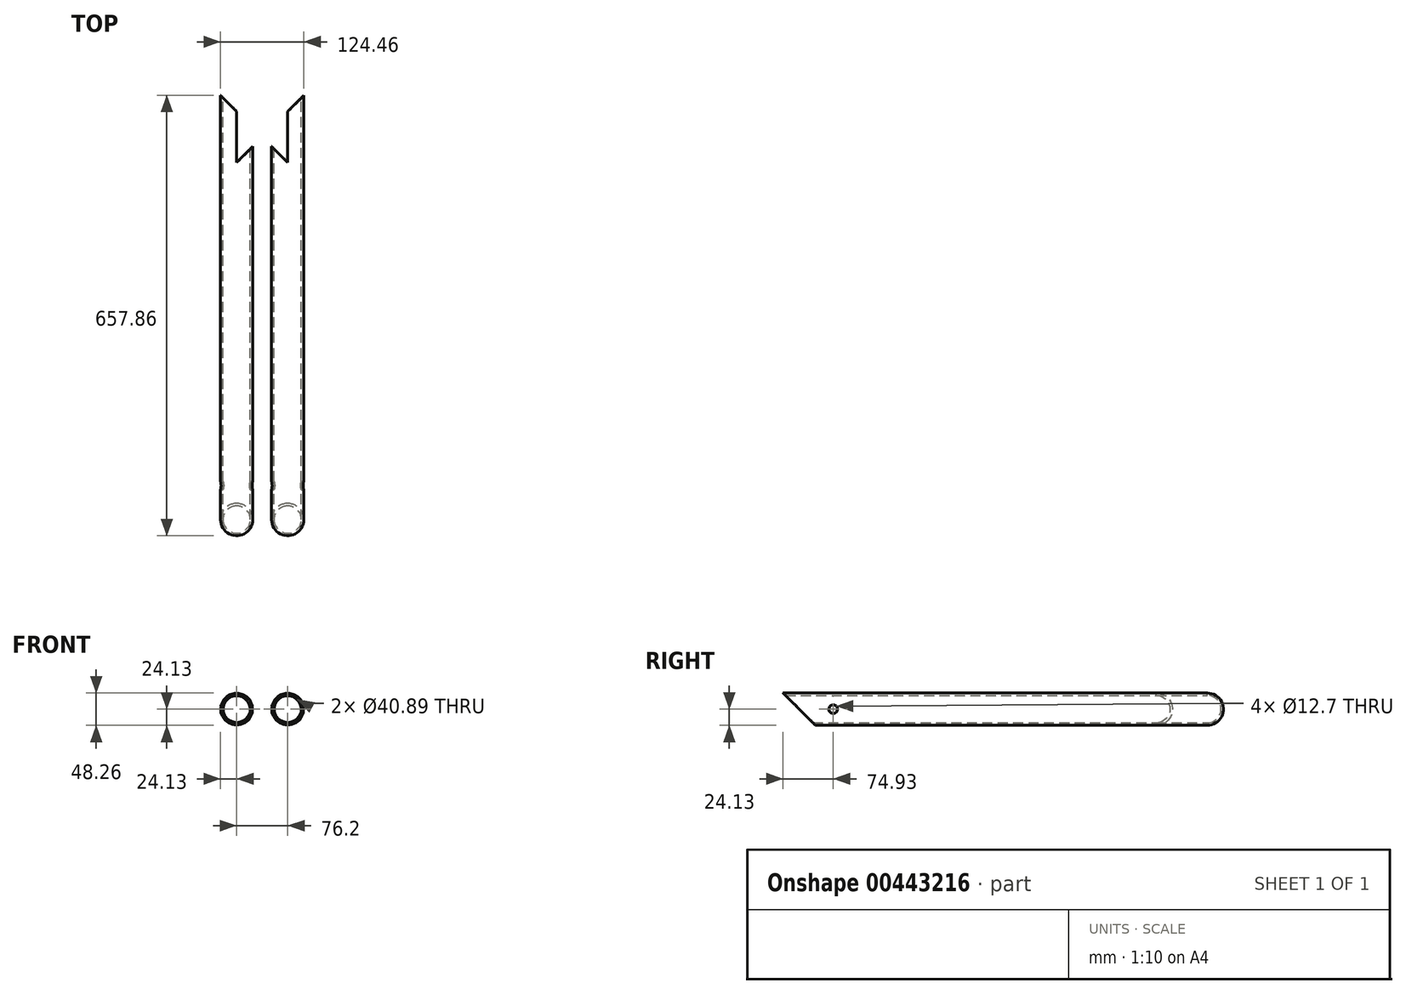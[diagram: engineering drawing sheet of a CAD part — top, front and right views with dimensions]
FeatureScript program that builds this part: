
annotation { "Feature Type Name" : "Feature", "Feature Type Description" : "" }
export const myFeature = defineFeature(function(context is Context, id is Id, definition is map)
    precondition{}
    {
        {
            var Q0;
            Q0=qCreatedBy(makeId("Front.planeOp"),FACE);
            var sketch = newSketch(context, id + "F0", { "sketchPlane" : qUnion([Q0])});
            skCircle(sketch, "E0", {"center": v(0, 0) * mm, "radius": 24.13 * mm});
            skCircle(sketch, "E1", {"center": v(0, 0) * mm, "radius": 20.45 * mm});
            skSolve(sketch);
        }
        {
            var Q0;
            Q0=makeQuery(id+"F0.imprint","IMPRINT",FACE,{"disambiguationData":[TD([[makeQuery(id+"F0.imprint","IMPRINT",EDGE,{"derivedFrom":sQuery(id+"F0.wireOp",EDGE,"E0")}),1.0]])]});
            extrude(context, id + "F1", {"entities" : qUnion([Q0]), "endBound" : BoundingType.SYMMETRIC, "depth" : 711.2 * mm});
        }
        {
            var Q0;
            Q0=qCreatedBy(makeId("Front.planeOp"),FACE);
            var sketch = newSketch(context, id + "F2", { "sketchPlane" : qUnion([Q0])});
            skCircle(sketch, "E2", {"center": v(-76.2, 0) * mm, "radius": 24.13 * mm});
            skCircle(sketch, "E3", {"center": v(-76.2, 0) * mm, "radius": 20.45 * mm});
            skSolve(sketch);
        }
        {
            var Q0;
            Q0=makeQuery(id+"F2.imprint","IMPRINT",FACE,{"disambiguationData":[TD([[makeQuery(id+"F2.imprint","IMPRINT",EDGE,{"derivedFrom":sQuery(id+"F2.wireOp",EDGE,"E2")}),1.0]])]});
            extrude(context, id + "F3", {"entities" : qUnion([Q0]), "endBound" : BoundingType.SYMMETRIC, "depth" : 711.2 * mm});
        }
        {
            var Q0;
            Q0=qCreatedBy(makeId("Right.planeOp"),FACE);
            var sketch = newSketch(context, id + "F4", { "sketchPlane" : qUnion([Q0])});
            skLineSegment(sketch, "E4", {"start": v(-304.8, 0) * mm, "end": v(-400.48, 95.68) * mm});
            skLineSegment(sketch, "E5", {"start": v(-400.48, 95.68) * mm, "end": v(-522.8, 95.68) * mm});
            skLineSegment(sketch, "E6", {"start": v(-522.8, 95.68) * mm, "end": v(-522.8, -148.2) * mm});
            skLineSegment(sketch, "E7", {"start": v(-522.8, -148.2) * mm, "end": v(-156.6, -148.2) * mm});
            skLineSegment(sketch, "E8", {"start": v(-156.6, -148.2) * mm, "end": v(-304.8, 0) * mm});
            skSolve(sketch);
        }
        {
            var Q0;
            Q0 = qSketchRegion(id + "F4", true);
            extrude(context, id + "F5", {"entities" : qUnion([Q0]), "operationType" : NewBodyOperationType.REMOVE, "endBound" : BoundingType.SYMMETRIC, "oppositeDirection" : true, "depth" : 304.8 * mm});
        }
        {
            var Q0;
            Q0=qCreatedBy(makeId("Top.planeOp"),FACE);
            var sketch = newSketch(context, id + "F6", { "sketchPlane" : qUnion([Q0])});
            skLineSegment(sketch, "E9", {"start": v(0, 304.8) * mm, "end": v(-76.2, 228.6) * mm});
            skLineSegment(sketch, "E10", {"start": v(-76.2, 228.6) * mm, "end": v(-76.2, 508) * mm});
            skLineSegment(sketch, "E11", {"start": v(-76.2, 508) * mm, "end": v(76.2, 508) * mm});
            skLineSegment(sketch, "E12", {"start": v(76.2, 508) * mm, "end": v(76.2, 381) * mm});
            skLineSegment(sketch, "E13", {"start": v(76.2, 381) * mm, "end": v(0, 304.8) * mm});
            skSolve(sketch);
        }
        {
            var Q0;
            Q0 = qSketchRegion(id + "F6", true);
            extrude(context, id + "F7", {"entities" : qUnion([Q0]), "operationType" : NewBodyOperationType.REMOVE, "endBound" : BoundingType.SYMMETRIC, "oppositeDirection" : true, "depth" : 152.4 * mm});
        }
        {
            var Q0;
            Q0=qCreatedBy(makeId("Top.planeOp"),FACE);
            var sketch = newSketch(context, id + "F8", { "sketchPlane" : qUnion([Q0])});
            skLineSegment(sketch, "E14", {"start": v(-76.2, 0) * mm, "end": v(-76.2, 397.11) * mm, "construction": true});
            skLineSegment(sketch, "E15", {"start": v(-76.2, 304.8) * mm, "end": v(-152.4, 381) * mm});
            skLineSegment(sketch, "E16", {"start": v(-152.4, 381) * mm, "end": v(-152.4, 508) * mm});
            skLineSegment(sketch, "E17", {"start": v(-152.4, 508) * mm, "end": v(0, 508) * mm});
            skLineSegment(sketch, "E18", {"start": v(0, 508) * mm, "end": v(0, 228.6) * mm});
            skLineSegment(sketch, "E19", {"start": v(0, 228.6) * mm, "end": v(-76.2, 304.8) * mm});
            skSolve(sketch);
        }
        {
            var Q0;
            Q0 = qSketchRegion(id + "F8", true);
            extrude(context, id + "F9", {"entities" : qUnion([Q0]), "operationType" : NewBodyOperationType.REMOVE, "endBound" : BoundingType.SYMMETRIC, "oppositeDirection" : true, "depth" : 152.4 * mm});
        }
        {
            var Q0;
            Q0=qCreatedBy(makeId("Right.planeOp"),FACE);
            var sketch = newSketch(context, id + "F10", { "sketchPlane" : qUnion([Q0])});
            skCircle(sketch, "E20", {"center": v(-254, 0) * mm, "radius": 6.35 * mm});
            skSolve(sketch);
        }
        {
            var Q0;
            Q0 = qSketchRegion(id + "F10", true);
            extrude(context, id + "F11", {"entities" : qUnion([Q0]), "operationType" : NewBodyOperationType.REMOVE, "endBound" : BoundingType.SYMMETRIC, "oppositeDirection" : true, "depth" : 304.8 * mm});
        }
    });
